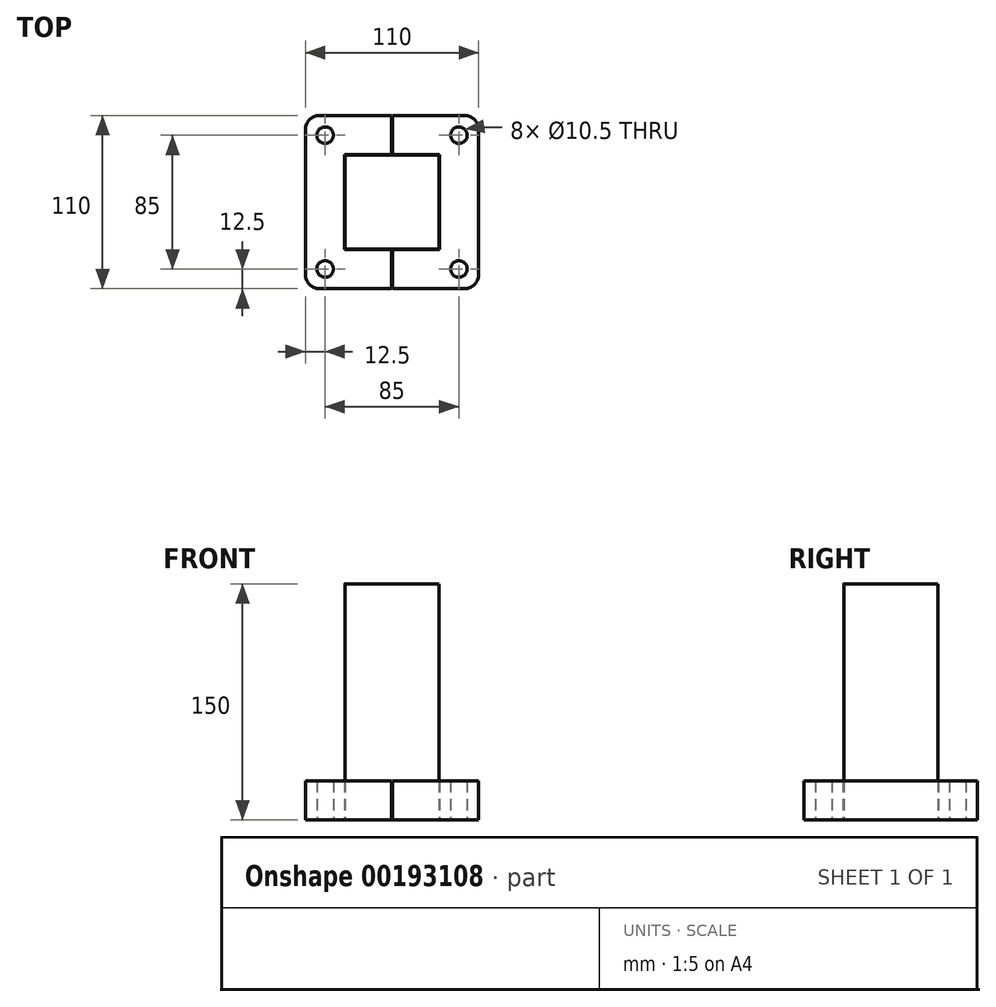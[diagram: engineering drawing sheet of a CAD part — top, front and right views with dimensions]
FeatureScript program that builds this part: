
annotation { "Feature Type Name" : "Feature", "Feature Type Description" : "" }
export const myFeature = defineFeature(function(context is Context, id is Id, definition is map)
    precondition{}
    {
        {
            var Q0;
            Q0=qCreatedBy(makeId("Top.planeOp"),FACE);
            var sketch = newSketch(context, id + "F0", { "sketchPlane" : qUnion([Q0])});
            skLineSegment(sketch, "E0.bottom", {"start": v(29.88, 29.88) * mm, "end": v(-29.88, 29.88) * mm, "construction": true});
            skLineSegment(sketch, "E0.top", {"start": v(29.88, -29.88) * mm, "end": v(-29.88, -29.88) * mm, "construction": true});
            skLineSegment(sketch, "E0.left", {"start": v(29.88, 29.88) * mm, "end": v(29.88, -29.88) * mm, "construction": true});
            skLineSegment(sketch, "E0.right", {"start": v(-29.88, 29.88) * mm, "end": v(-29.88, -29.88) * mm, "construction": true});
            skPoint(sketch, "E0.middle", {"position": v(0, 0) * mm});
            skLineSegment(sketch, "E1.0", {"start": v(30.28, 30.28) * mm, "end": v(0.2, 30.28) * mm});
            skLineSegment(sketch, "E1.1", {"start": v(30.28, 30.28) * mm, "end": v(30.28, 0) * mm});
            skLineSegment(sketch, "E2", {"start": v(0, 29.88) * mm, "end": v(0, -29.88) * mm, "construction": true});
            skLineSegment(sketch, "E3", {"start": v(0.2, 30.28) * mm, "end": v(0.2, 55) * mm});
            skLineSegment(sketch, "E4", {"start": v(0.2, 55) * mm, "end": v(55, 55) * mm});
            skLineSegment(sketch, "E5", {"start": v(55, 55) * mm, "end": v(55, 0) * mm});
            skLineSegment(sketch, "E6", {"start": v(55, 55) * mm, "end": v(0, 55) * mm, "construction": true});
            skLineSegment(sketch, "E7.MirrorCS", {"start": v(55, -55) * mm, "end": v(55, 0) * mm});
            skLineSegment(sketch, "E8.MirrorCS", {"start": v(30.28, -30.28) * mm, "end": v(30.28, 0) * mm});
            skLineSegment(sketch, "E9.MirrorCS", {"start": v(30.28, -30.28) * mm, "end": v(0.2, -30.28) * mm});
            skLineSegment(sketch, "E10.MirrorCS", {"start": v(0.2, -30.28) * mm, "end": v(0.2, -55) * mm});
            skLineSegment(sketch, "E11", {"start": v(0.2, -55) * mm, "end": v(55, -55) * mm});
            skLineSegment(sketch, "E12", {"start": v(0, 0) * mm, "end": v(55, 55) * mm, "construction": true});
            skCircle(sketch, "E13", {"center": v(42.5, 42.5) * mm, "radius": 5.25 * mm});
            skCircle(sketch, "E14.MirrorC", {"center": v(42.5, -42.5) * mm, "radius": 5.25 * mm});
            skSolve(sketch);
        }
        {
            var Q0;
            Q0=makeQuery(id+"F0.imprint","IMPRINT",FACE,{"disambiguationData":[TD([[makeQuery(id+"F0.imprint","IMPRINT",EDGE,{"derivedFrom":sQuery(id+"F0.wireOp",EDGE,"E1.0")}),-1.0]])]});
            extrude(context, id + "F1", {"entities" : qUnion([Q0]), "depth" : 25 * mm});
        }
        {
            var Q0;
            Q0=makeQuery(id+"F1.opExtrude","SWEPT_EDGE",EDGE,{"disambiguationData":[OSD([sQuery(id+"F0.wireOp",EDGE,"E7.MirrorCS"),sQuery(id+"F0.wireOp",EDGE,"E11")])]});
            var Q1;
            Q1=makeQuery(id+"F1.opExtrude","SWEPT_EDGE",EDGE,{"disambiguationData":[OSD([sQuery(id+"F0.wireOp",EDGE,"E4"),sQuery(id+"F0.wireOp",EDGE,"E5")])]});
            fillet(context, id + "F2", {"entities" : qUnion([Q0, Q1]), "radius" : 9 * mm, "tangentPropagation" : true, "allowEdgeOverflow" : false});
        }
        {
            var Q0;
            Q0=makeQuery(id+"F1.opExtrude","SWEPT_BODY",BODY,{"disambiguationData":[OSD([sQuery(id+"F0.wireOp",EDGE,"E1.0"),sQuery(id+"F0.wireOp",EDGE,"E1.1"),sQuery(id+"F0.wireOp",EDGE,"E3"),sQuery(id+"F0.wireOp",EDGE,"E4"),sQuery(id+"F0.wireOp",EDGE,"E5"),sQuery(id+"F0.wireOp",EDGE,"E7.MirrorCS"),sQuery(id+"F0.wireOp",EDGE,"E8.MirrorCS"),sQuery(id+"F0.wireOp",EDGE,"E9.MirrorCS"),sQuery(id+"F0.wireOp",EDGE,"E10.MirrorCS"),sQuery(id+"F0.wireOp",EDGE,"E11"),sQuery(id+"F0.wireOp",EDGE,"E13"),sQuery(id+"F0.wireOp",EDGE,"E14.MirrorC")])]});
            var Q1;
            Q1=qCreatedBy(makeId("Right.planeOp"),FACE);
            mirror(context, id + "F3", {"entities" : qUnion([Q0]), "mirrorPlane" : qUnion([Q1])});
        }
        {
            var Q0;
            Q0=qCreatedBy(makeId("Top.planeOp"),FACE);
            var sketch = newSketch(context, id + "F4", { "sketchPlane" : qUnion([Q0])});
            skLineSegment(sketch, "E15.0", {"start": v(-29.88, 29.88) * mm, "end": v(-29.88, -29.88) * mm});
            skLineSegment(sketch, "E16.0", {"start": v(29.88, 29.88) * mm, "end": v(-29.88, 29.88) * mm});
            skLineSegment(sketch, "E17.0", {"start": v(29.88, 29.88) * mm, "end": v(29.88, -29.88) * mm});
            skLineSegment(sketch, "E18.0", {"start": v(29.88, -29.88) * mm, "end": v(-29.88, -29.88) * mm});
            skSolve(sketch);
        }
        {
            var Q0;
            Q0 = qSketchRegion(id + "F4", true);
            extrude(context, id + "F5", {"entities" : qUnion([Q0]), "depth" : 150 * mm});
        }
        {
            var Q0;
            Q0=makeQuery(id+"F5.opExtrude","SWEPT_EDGE",EDGE,{"disambiguationData":[OSD([sQuery(id+"F4.wireOp",EDGE,"E15.0"),sQuery(id+"F4.wireOp",EDGE,"E18.0")])]});
            var Q1;
            Q1=makeQuery(id+"F5.opExtrude","SWEPT_EDGE",EDGE,{"disambiguationData":[OSD([sQuery(id+"F4.wireOp",EDGE,"E15.0"),sQuery(id+"F4.wireOp",EDGE,"E16.0")])]});
            var Q2;
            Q2=makeQuery(id+"F5.opExtrude","SWEPT_EDGE",EDGE,{"disambiguationData":[OSD([sQuery(id+"F4.wireOp",EDGE,"E17.0"),sQuery(id+"F4.wireOp",EDGE,"E18.0")])]});
            var Q3;
            Q3=makeQuery(id+"F5.opExtrude","SWEPT_EDGE",EDGE,{"disambiguationData":[OSD([sQuery(id+"F4.wireOp",EDGE,"E16.0"),sQuery(id+"F4.wireOp",EDGE,"E17.0")])]});
            fillet(context, id + "F6", {"entities" : qUnion([Q0, Q1, Q2, Q3]), "radius" : 1 * mm, "tangentPropagation" : true, "allowEdgeOverflow" : false});
        }
    });
